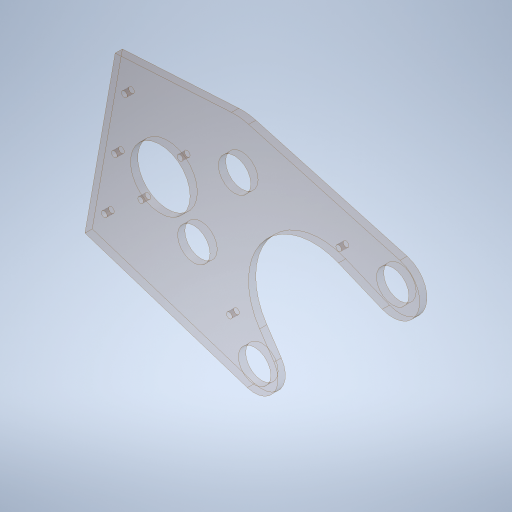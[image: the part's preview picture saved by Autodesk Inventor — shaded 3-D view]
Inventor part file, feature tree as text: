
AUTODESK INVENTOR PART (.ipt)
format: ipt  version: 2023.4 (Build 274418000, 418)  size: 353,792 bytes
history: native  units: in
note: dims shown in document units (in); Inventor stores cm internally (conversion verified against a paired STEP export)
features: sketch x1, extrude x1, hole x1
ambient origin geometry x8: Origin, YZ Plane, XZ Plane, XY Plane, X Axis, Y Axis, Z Axis, Center Point
bodies: Solid1 (feature_tree)
feature tree (3):
  sketch  "Sketch1"  dims[d3=45.0deg d4=0.0in d7=2.0in d8=4.25in d9=1.125in d10=3.0in d11=4.5in d12=4.5in d13=0.25in d14=0.375in d15=5.499in d16=1.128in d17=3.341in d18=3.126in d19=3.126in d22=1.0in d23=6.0in d26=8.0293in d27=2.0in d28=0.4688in d29=0.3504in d30=6.75in d31=0.0687in d32=0.75in d33=4.0in d34=1.375in d35=0.75in d36=0.25in d37=1.375in d38=2.3622in d40=360.0deg d43=0.1718in d44=0.375in d45=0.25in d46=0.0in d47=0.201in d48=0.75in d49=0.37in d50=0.25in d51=90.0deg d52=1.0in d53=0.8108in d54=0.3in d55=0.5497in d57=3.1875in d59=0.0312in]
  extrude  "Extrusion1"  TaperAngle=0.0deg  [1 undecoded]
  hole  "Hole1"  [1 undecoded]
note: 2 required parameter values undecoded (feature->parameter linkage not recoverable at this tier; creation-order binding heuristic only, values carry confidence <= 0.55)
